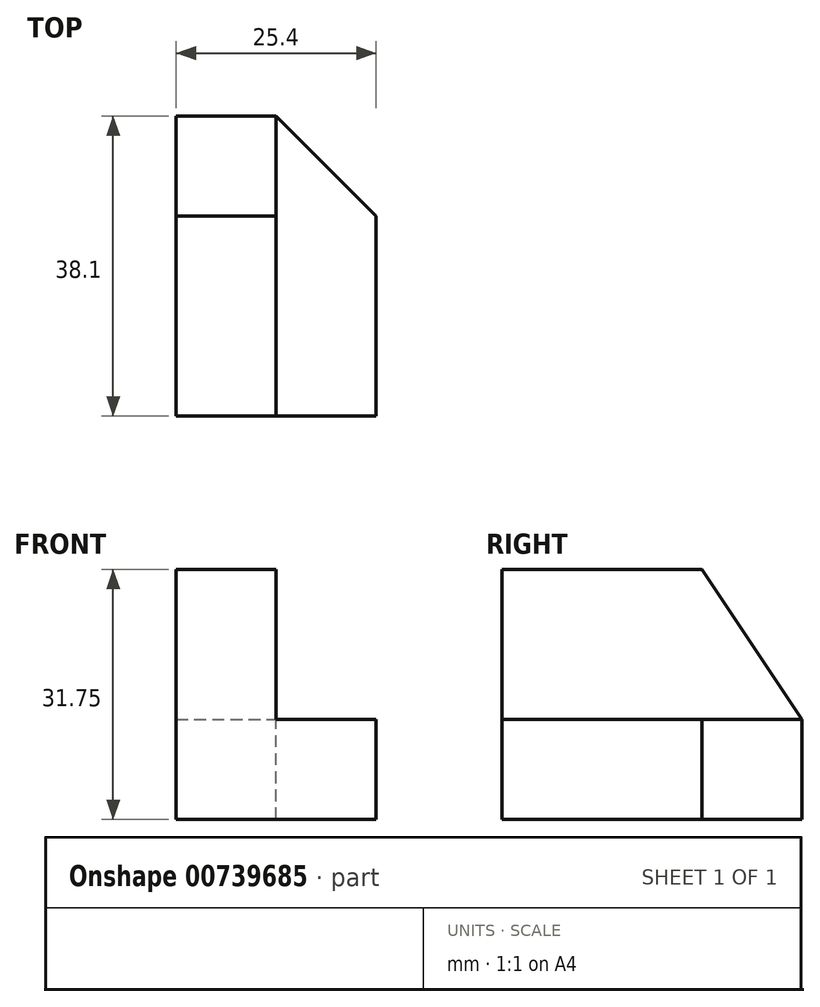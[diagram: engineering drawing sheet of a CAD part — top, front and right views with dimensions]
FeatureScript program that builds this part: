
annotation { "Feature Type Name" : "Feature", "Feature Type Description" : "" }
export const myFeature = defineFeature(function(context is Context, id is Id, definition is map)
    precondition{}
    {
        {
            var Q0;
            Q0=qCreatedBy(makeId("Front.planeOp"),FACE);
            var sketch = newSketch(context, id + "F0", { "sketchPlane" : qUnion([Q0])});
            skLineSegment(sketch, "E0.bottom", {"start": v(0, 0) * mm, "end": v(25.4, 0) * mm});
            skLineSegment(sketch, "E0.top", {"start": v(0, 31.75) * mm, "end": v(25.4, 31.75) * mm});
            skLineSegment(sketch, "E0.left", {"start": v(0, 0) * mm, "end": v(0, 31.75) * mm});
            skLineSegment(sketch, "E0.right", {"start": v(25.4, 0) * mm, "end": v(25.4, 31.75) * mm});
            skSolve(sketch);
        }
        {
            var Q0;
            Q0 = qSketchRegion(id + "F0", true);
            extrude(context, id + "F1", {"entities" : qUnion([Q0]), "depth" : 38.1 * mm, "offsetDistance" : 25.4 * mm});
        }
        {
            var Q0;
            Q0=makeQuery(id+"F1.opExtrude","CAP_FACE",FACE,{"disambiguationData":[OSD([sQuery(id+"F0.wireOp",EDGE,"E0.bottom"),sQuery(id+"F0.wireOp",EDGE,"E0.top"),sQuery(id+"F0.wireOp",EDGE,"E0.left"),sQuery(id+"F0.wireOp",EDGE,"E0.right")])],"isStart":true});
            var sketch = newSketch(context, id + "F2", { "sketchPlane" : qUnion([Q0])});
            skLineSegment(sketch, "E1", {"start": v(-25.4, 31.75) * mm, "end": v(-25.4, 12.7) * mm});
            skLineSegment(sketch, "E2", {"start": v(-25.4, 31.75) * mm, "end": v(-12.7, 31.75) * mm});
            skLineSegment(sketch, "E3", {"start": v(-25.4, 12.7) * mm, "end": v(-12.7, 12.7) * mm});
            skLineSegment(sketch, "E4", {"start": v(-12.7, 31.75) * mm, "end": v(-12.7, 12.7) * mm});
            skSolve(sketch);
        }
        {
            var Q0;
            Q0 = qSketchRegion(id + "F2", true);
            extrude(context, id + "F3", {"entities" : qUnion([Q0]), "operationType" : NewBodyOperationType.REMOVE, "oppositeDirection" : true, "depth" : 38.1 * mm, "offsetDistance" : 25.4 * mm});
        }
        {
            var Q0;
            Q0=makeQuery(id+"F3.boolean.opBoolean","COPY",FACE,{"derivedFrom":makeQuery(id+"F3.opExtrude","SWEPT_FACE",FACE,{"disambiguationData":[OSD([sQuery(id+"F2.wireOp",EDGE,"E4")])]})});
            var sketch = newSketch(context, id + "F4", { "sketchPlane" : qUnion([Q0])});
            skLineSegment(sketch, "E5", {"start": v(0, 31.75) * mm, "end": v(-12.7, 31.75) * mm});
            skLineSegment(sketch, "E6", {"start": v(0, 31.75) * mm, "end": v(0, 12.7) * mm});
            skLineSegment(sketch, "E7", {"start": v(-12.7, 31.75) * mm, "end": v(0, 12.7) * mm});
            skSolve(sketch);
        }
        {
            var Q0;
            Q0 = qSketchRegion(id + "F4", true);
            extrude(context, id + "F5", {"entities" : qUnion([Q0]), "operationType" : NewBodyOperationType.REMOVE, "oppositeDirection" : true, "depth" : 25.4 * mm, "offsetDistance" : 25.4 * mm});
        }
        {
            var Q0;
            Q0=makeQuery(id+"F3.boolean.opBoolean","COPY",FACE,{"derivedFrom":makeQuery(id+"F3.opExtrude","SWEPT_FACE",FACE,{"disambiguationData":[OSD([sQuery(id+"F2.wireOp",EDGE,"E3")])]})});
            var sketch = newSketch(context, id + "F6", { "sketchPlane" : qUnion([Q0])});
            skLineSegment(sketch, "E8", {"start": v(25.4, -12.7) * mm, "end": v(25.4, 0) * mm});
            skLineSegment(sketch, "E9", {"start": v(25.4, 0) * mm, "end": v(12.7, 0) * mm});
            skLineSegment(sketch, "E10", {"start": v(12.7, 0) * mm, "end": v(25.4, -12.7) * mm});
            skSolve(sketch);
        }
        {
            var Q0;
            Q0 = qSketchRegion(id + "F6", true);
            extrude(context, id + "F7", {"entities" : qUnion([Q0]), "operationType" : NewBodyOperationType.REMOVE, "oppositeDirection" : true, "depth" : 25.4 * mm, "offsetDistance" : 25.4 * mm});
        }
    });
